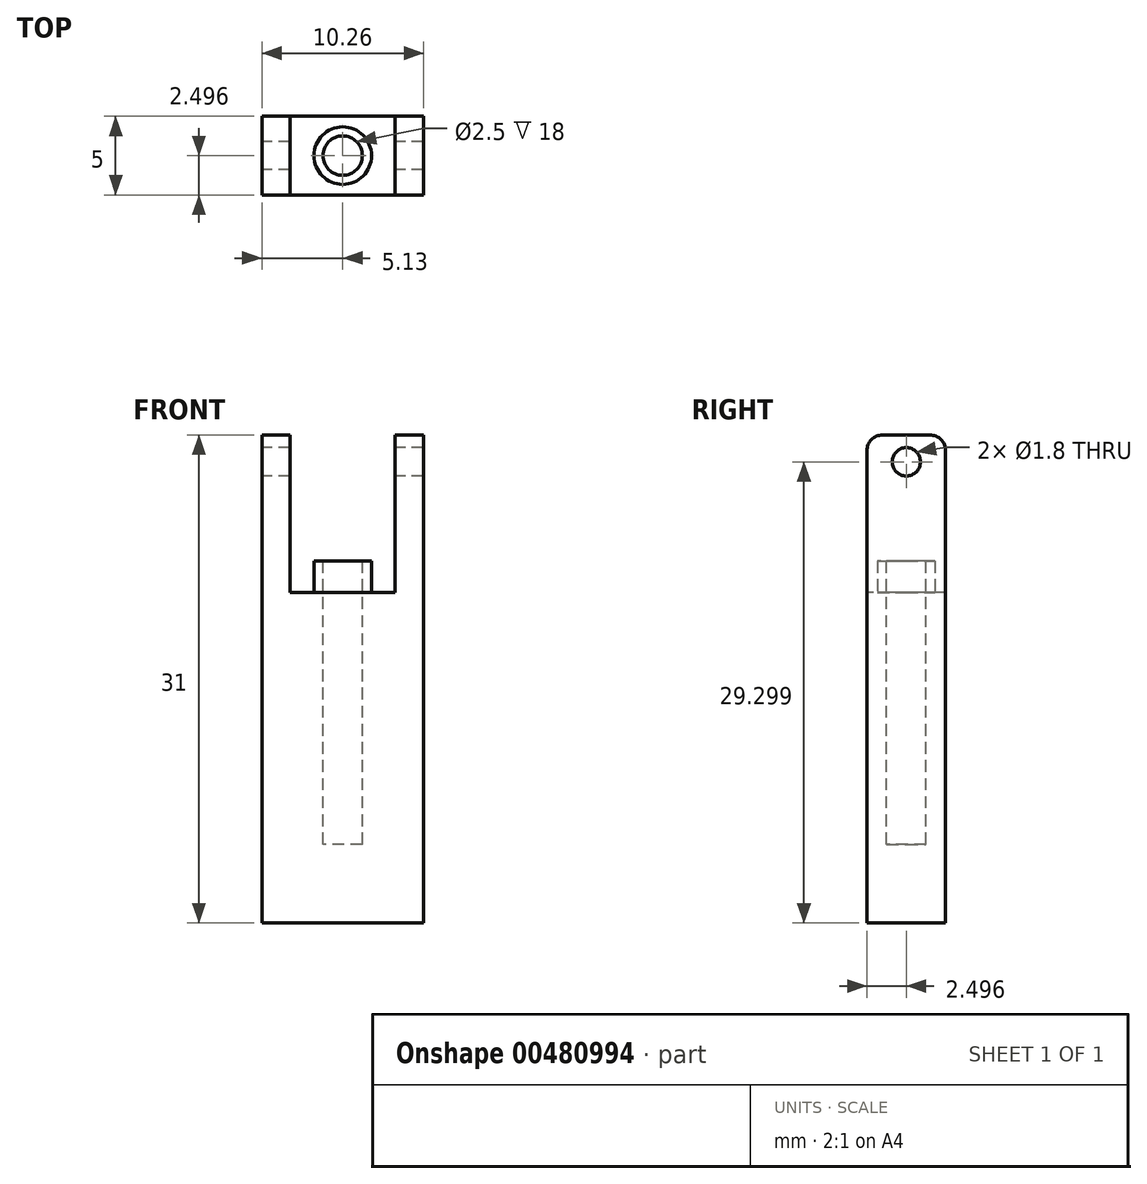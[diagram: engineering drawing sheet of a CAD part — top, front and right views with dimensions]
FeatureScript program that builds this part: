
annotation { "Feature Type Name" : "Feature", "Feature Type Description" : "" }
export const myFeature = defineFeature(function(context is Context, id is Id, definition is map)
    precondition{}
    {
        {
            var Q0;
            Q0=qCreatedBy(makeId("Right.planeOp"),FACE);
            var sketch = newSketch(context, id + "F0", { "sketchPlane" : qUnion([Q0])});
            skLineSegment(sketch, "E0", {"start": v(-22.47, 25.96) * mm, "end": v(-19.47, 25.96) * mm});
            skLineSegment(sketch, "E1", {"start": v(-23.47, 24.96) * mm, "end": v(-23.47, 15.96) * mm});
            skLineSegment(sketch, "E2", {"start": v(-18.47, 24.96) * mm, "end": v(-18.47, 15.96) * mm});
            skLineSegment(sketch, "E3", {"start": v(-18.47, 15.96) * mm, "end": v(-23.47, 15.96) * mm});
            skLineSegment(sketch, "E4", {"start": v(-20.97, 25.96) * mm, "end": v(-20.97, 25.16) * mm, "construction": true});
            skCircle(sketch, "E5", {"center": v(-20.97, 24.26) * mm, "radius": 0.9 * mm});
            skLineSegment(sketch, "E6.trimOffspring", {"start": v(-20.97, 23.36) * mm, "end": v(-20.97, 15.96) * mm, "construction": true});
            skPoint(sketch, "E7.visualSharp", {"position": v(-23.47, 25.96) * mm});
            skArc(sketch, "E7.filletArc", {"start": v(-22.47, 25.96) * mm, "mid": v(-23.18, 25.67) * mm, "end": v(-23.47, 24.96) * mm});
            skPoint(sketch, "E8.visualSharp", {"position": v(-18.47, 25.96) * mm});
            skArc(sketch, "E8.filletArc", {"start": v(-18.47, 24.96) * mm, "mid": v(-18.77, 25.67) * mm, "end": v(-19.47, 25.96) * mm});
            skSolve(sketch);
        }
        {
            var Q0;
            Q0=makeQuery(id+"F0.imprint","IMPRINT",FACE,{"disambiguationData":[TD([[makeQuery(id+"F0.imprint","IMPRINT",EDGE,{"derivedFrom":sQuery(id+"F0.wireOp",EDGE,"E0")}),-1.0]])]});
            extrude(context, id + "F1", {"entities" : qUnion([Q0]), "depth" : 1.8 * mm});
        }
        {
            var Q0;
            Q0=makeQuery(id+"F1.opExtrude","SWEPT_FACE",FACE,{"disambiguationData":[OSD([sQuery(id+"F0.wireOp",EDGE,"E3")])]});
            extrude(context, id + "F2", {"entities" : qUnion([Q0]), "operationType" : NewBodyOperationType.ADD, "depth" : 2 * mm});
        }
        {
            var Q0;
            {var subQ0=sQuery(id+"F0.wireOp",EDGE,"E3");Q0=makeQuery(id+"F2.boolean.opBoolean","MERGE",FACE,{"derivedFrom":[makeQuery(id+"F1.opExtrude","CAP_FACE",FACE,{"disambiguationData":[OSD([sQuery(id+"F0.wireOp",EDGE,"E0"),sQuery(id+"F0.wireOp",EDGE,"E1"),sQuery(id+"F0.wireOp",EDGE,"E2"),subQ0,sQuery(id+"F0.wireOp",EDGE,"E5"),sQuery(id+"F0.wireOp",EDGE,"E7.filletArc"),sQuery(id+"F0.wireOp",EDGE,"E8.filletArc")])],"isStart":true}),makeQuery(id+"F2.opExtrude","SWEPT_FACE",FACE,{"disambiguationData":[OSD([subQ0]),TDD([makeQuery(id+"F1.opExtrude","CAP_EDGE",EDGE,{"disambiguationData":[OSD([subQ0])],"isStart":true})])]})]});}
            var sketch = newSketch(context, id + "F3", { "sketchPlane" : qUnion([Q0])});
            skLineSegment(sketch, "E9", {"start": v(18.47, 13.96) * mm, "end": v(18.47, 15.96) * mm});
            skLineSegment(sketch, "E10", {"start": v(18.47, 15.96) * mm, "end": v(23.47, 15.96) * mm});
            skSolve(sketch);
        }
        {
            var Q0;
            Q0=makeQuery(id+"F1.opExtrude","SWEPT_BODY",BODY,{"disambiguationData":[OSD([sQuery(id+"F0.wireOp",EDGE,"E0"),sQuery(id+"F0.wireOp",EDGE,"E1"),sQuery(id+"F0.wireOp",EDGE,"E2"),sQuery(id+"F0.wireOp",EDGE,"E3"),sQuery(id+"F0.wireOp",EDGE,"E5"),sQuery(id+"F0.wireOp",EDGE,"E7.filletArc"),sQuery(id+"F0.wireOp",EDGE,"E8.filletArc")])]});
            transform(context, id + "F4", {"entities" : qUnion([Q0]), "transformType" : TransformType.TRANSLATION_3D, "dx" : -8.46 * mm, "dy" : 0 * mm, "dz" : 0 * mm, "makeCopy" : true});
        }
        {
            var Q0;
            Q0=makeQuery(id+"F3.imprint","IMPRINT",FACE,{"disambiguationData":[TD([[makeQuery(id+"F3.imprint","IMPRINT",EDGE,{"derivedFrom":sQuery(id+"F3.wireOp",EDGE,"E9")}),1.0]])]});
            extrude(context, id + "F5", {"entities" : qUnion([Q0]), "operationType" : NewBodyOperationType.ADD, "depth" : 6.66 * mm});
        }
        {
            var Q0;
            {var subQ0=sQuery(id+"F0.wireOp",EDGE,"E3");var subQ1=makeQuery(id+"F2.opExtrude","CAP_FACE",FACE,{"disambiguationData":[OSD([subQ0])],"isStart":false});Q0=makeQuery(id+"F5.boolean.opBoolean","MERGE",FACE,{"derivedFrom":[subQ1,makeQuery(id+"F4.opPattern","COPY",FACE,{"derivedFrom":subQ1,"instanceName":"1"}),makeQuery(id+"F5.opExtrude","SWEPT_FACE",FACE,{"disambiguationData":[OSD([subQ0])]})]});}
            var sketch = newSketch(context, id + "F6", { "sketchPlane" : qUnion([Q0])});
            skCircle(sketch, "E11", {"center": v(-3.33, 20.97) * mm, "radius": 1.83 * mm});
            skSolve(sketch);
        }
        {
            var Q0;
            Q0=makeQuery(id+"F6.imprint","IMPRINT",FACE,{"disambiguationData":[TD([[makeQuery(id+"F6.imprint","IMPRINT",EDGE,{"derivedFrom":sQuery(id+"F6.wireOp",EDGE,"E11")}),1.0]])]});
            extrude(context, id + "F7", {"entities" : qUnion([Q0]), "operationType" : NewBodyOperationType.ADD, "depth" : 19 * mm});
        }
        {
            var Q0;
            Q0=makeQuery(id+"F5.opExtrude","SWEPT_FACE",FACE,{"disambiguationData":[OSD([sQuery(id+"F3.wireOp",EDGE,"E10")])]});
            var sketch = newSketch(context, id + "F8", { "sketchPlane" : qUnion([Q0])});
            skLineSegment(sketch, "E12", {"start": v(-3.33, -18.47) * mm, "end": v(-3.33, -23.47) * mm, "construction": true});
            skLineSegment(sketch, "E13", {"start": v(0, -20.97) * mm, "end": v(-6.66, -20.97) * mm, "construction": true});
            skCircle(sketch, "E14", {"center": v(-3.33, -20.97) * mm, "radius": 1.25 * mm});
            skSolve(sketch);
        }
        {
            var Q0;
            Q0=makeQuery(id+"F8.imprint","IMPRINT",FACE,{"disambiguationData":[TD([[makeQuery(id+"F8.imprint","IMPRINT",EDGE,{"derivedFrom":sQuery(id+"F8.wireOp",EDGE,"E14")}),1.0]])]});
            extrude(context, id + "F9", {"entities" : qUnion([Q0]), "operationType" : NewBodyOperationType.REMOVE, "oppositeDirection" : true, "depth" : 16 * mm});
        }
        {
            var Q0;
            {var subQ0=sQuery(id+"F0.wireOp",EDGE,"E3");var subQ1=makeQuery(id+"F2.opExtrude","CAP_FACE",FACE,{"disambiguationData":[OSD([subQ0])],"isStart":false});Q0=makeQuery(id+"F5.boolean.opBoolean","MERGE",FACE,{"derivedFrom":[subQ1,makeQuery(id+"F4.opPattern","COPY",FACE,{"derivedFrom":subQ1,"instanceName":"1"}),makeQuery(id+"F5.opExtrude","SWEPT_FACE",FACE,{"disambiguationData":[OSD([subQ0])]})]});}
            extrude(context, id + "F10", {"entities" : qUnion([Q0]), "operationType" : NewBodyOperationType.ADD, "depth" : 19 * mm});
        }
        {
            var Q0;
            Q0=makeQuery(id+"F5.opExtrude","SWEPT_FACE",FACE,{"disambiguationData":[OSD([sQuery(id+"F3.wireOp",EDGE,"E10")])]});
            var sketch = newSketch(context, id + "F11", { "sketchPlane" : qUnion([Q0])});
            skCircle(sketch, "E15", {"center": v(-3.33, -20.97) * mm, "radius": 1.83 * mm});
            skSolve(sketch);
        }
        {
            var Q0;
            Q0=makeQuery(id+"F11.imprint","IMPRINT",FACE,{"disambiguationData":[TD([[makeQuery(id+"F11.imprint","IMPRINT",EDGE,{"derivedFrom":sQuery(id+"F11.wireOp",EDGE,"E15")}),1.0]])]});
            extrude(context, id + "F12", {"entities" : qUnion([Q0]), "operationType" : NewBodyOperationType.ADD, "depth" : 2 * mm});
        }
    });
